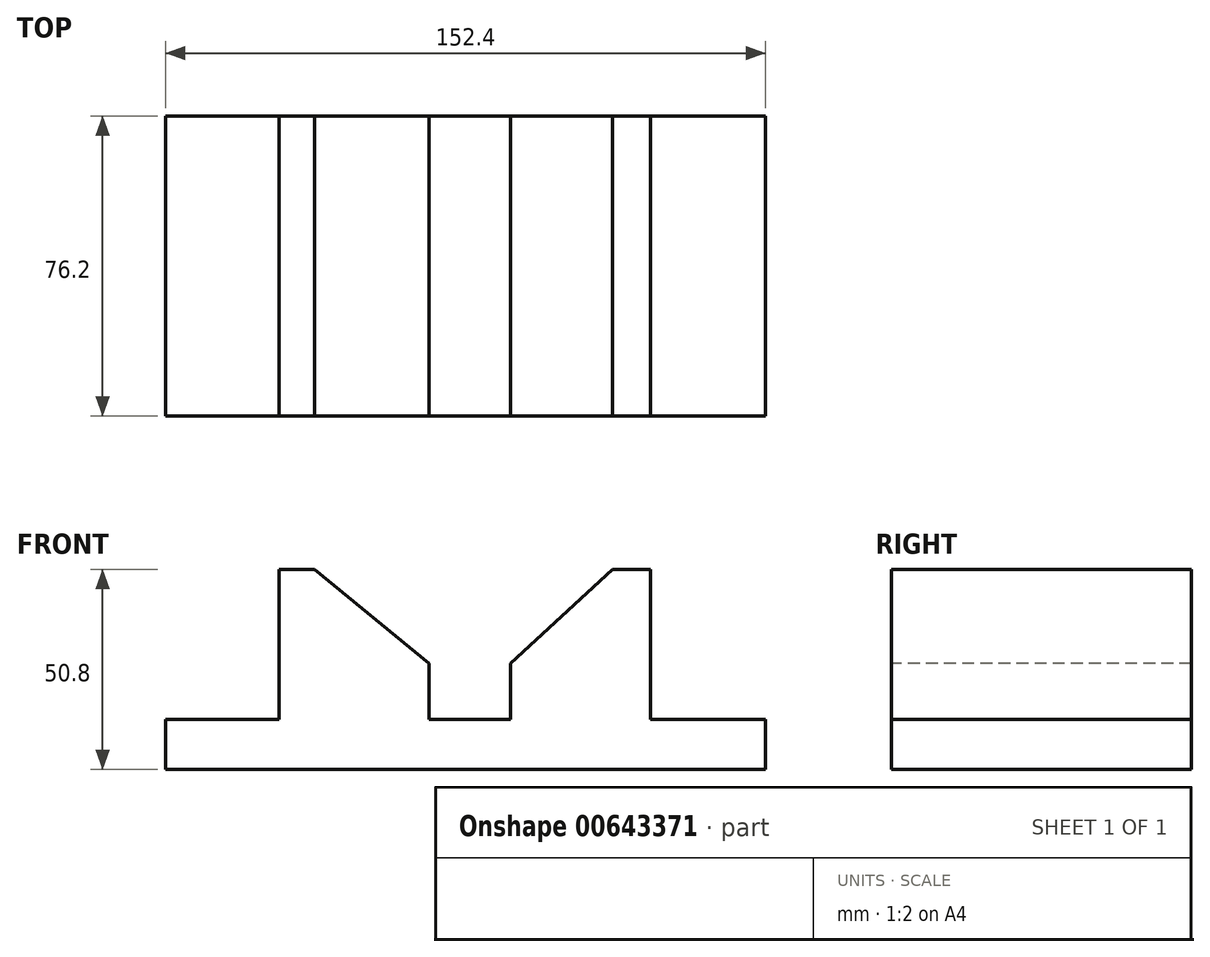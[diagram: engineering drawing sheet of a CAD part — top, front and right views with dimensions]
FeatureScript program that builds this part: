
annotation { "Feature Type Name" : "Feature", "Feature Type Description" : "" }
export const myFeature = defineFeature(function(context is Context, id is Id, definition is map)
    precondition{}
    {
        {
            var Q0;
            Q0=qCreatedBy(makeId("Top.planeOp"),FACE);
            var sketch = newSketch(context, id + "F0", { "sketchPlane" : qUnion([Q0])});
            skLineSegment(sketch, "E0.bottom", {"start": v(106.06, -5.27) * mm, "end": v(258.46, -5.27) * mm});
            skLineSegment(sketch, "E0.top", {"start": v(106.06, 70.93) * mm, "end": v(258.46, 70.93) * mm});
            skLineSegment(sketch, "E0.left", {"start": v(106.06, -5.27) * mm, "end": v(106.06, 70.93) * mm});
            skLineSegment(sketch, "E0.right", {"start": v(258.46, -5.27) * mm, "end": v(258.46, 70.93) * mm});
            skSolve(sketch);
        }
        {
            var Q0;
            Q0=makeQuery(id+"F0.imprint","IMPRINT",FACE,{"disambiguationData":[TD([[makeQuery(id+"F0.imprint","IMPRINT",EDGE,{"derivedFrom":sQuery(id+"F0.wireOp",EDGE,"E0.bottom")}),1.0]])]});
            extrude(context, id + "F1", {"entities" : qUnion([Q0]), "depth" : 12.7 * mm, "offsetDistance" : 25.4 * mm});
        }
        {
            var Q0;
            Q0=makeQuery(id+"F1.opExtrude","SWEPT_FACE",FACE,{"disambiguationData":[OSD([sQuery(id+"F0.wireOp",EDGE,"E0.bottom")])]});
            var sketch = newSketch(context, id + "F2", { "sketchPlane" : qUnion([Q0])});
            skLineSegment(sketch, "E1.bottom", {"start": v(134.92, 12.7) * mm, "end": v(173.02, 12.7) * mm});
            skLineSegment(sketch, "E1.top", {"start": v(134.92, 50.8) * mm, "end": v(173.02, 50.8) * mm});
            skLineSegment(sketch, "E1.left", {"start": v(134.92, 12.7) * mm, "end": v(134.92, 50.8) * mm});
            skLineSegment(sketch, "E1.right", {"start": v(173.02, 12.7) * mm, "end": v(173.02, 50.8) * mm});
            skSolve(sketch);
        }
        {
            var Q0;
            Q0=makeQuery(id+"F2.imprint","IMPRINT",FACE,{"disambiguationData":[TD([[makeQuery(id+"F2.imprint","IMPRINT",EDGE,{"derivedFrom":sQuery(id+"F2.wireOp",EDGE,"E1.bottom")}),1.0]])]});
            extrude(context, id + "F3", {"entities" : qUnion([Q0]), "operationType" : NewBodyOperationType.ADD, "oppositeDirection" : true, "depth" : 76.2 * mm, "offsetDistance" : 25.4 * mm});
        }
        {
            var Q0;
            Q0=makeQuery(id+"F3.boolean.opBoolean","MERGE",FACE,{"derivedFrom":[makeQuery(id+"F1.opExtrude","SWEPT_FACE",FACE,{"disambiguationData":[OSD([sQuery(id+"F0.wireOp",EDGE,"E0.bottom")])]}),makeQuery(id+"F3.opExtrude","CAP_FACE",FACE,{"disambiguationData":[OSD([sQuery(id+"F2.wireOp",EDGE,"E1.bottom"),sQuery(id+"F2.wireOp",EDGE,"E1.top"),sQuery(id+"F2.wireOp",EDGE,"E1.left"),sQuery(id+"F2.wireOp",EDGE,"E1.right")])],"isStart":true})]});
            var sketch = newSketch(context, id + "F4", { "sketchPlane" : qUnion([Q0])});
            skLineSegment(sketch, "E2.bottom", {"start": v(193.72, 12.7) * mm, "end": v(229.28, 12.7) * mm});
            skLineSegment(sketch, "E2.top", {"start": v(193.72, 50.8) * mm, "end": v(229.28, 50.8) * mm});
            skLineSegment(sketch, "E2.left", {"start": v(193.72, 12.7) * mm, "end": v(193.72, 50.8) * mm});
            skLineSegment(sketch, "E2.right", {"start": v(229.28, 12.7) * mm, "end": v(229.28, 50.8) * mm});
            skSolve(sketch);
        }
        {
            var Q0;
            Q0=makeQuery(id+"F4.imprint","IMPRINT",FACE,{"disambiguationData":[TD([[makeQuery(id+"F4.imprint","IMPRINT",EDGE,{"derivedFrom":sQuery(id+"F4.wireOp",EDGE,"E2.bottom")}),1.0]])]});
            extrude(context, id + "F5", {"entities" : qUnion([Q0]), "operationType" : NewBodyOperationType.ADD, "oppositeDirection" : true, "depth" : 76.2 * mm, "offsetDistance" : 25.4 * mm});
        }
        {
            var Q0;
            Q0=makeQuery(id+"F5.boolean.opBoolean","MERGE",FACE,{"derivedFrom":[makeQuery(id+"F3.boolean.opBoolean","MERGE",FACE,{"derivedFrom":[makeQuery(id+"F1.opExtrude","SWEPT_FACE",FACE,{"disambiguationData":[OSD([sQuery(id+"F0.wireOp",EDGE,"E0.bottom")])]}),makeQuery(id+"F3.opExtrude","CAP_FACE",FACE,{"disambiguationData":[OSD([sQuery(id+"F2.wireOp",EDGE,"E1.bottom"),sQuery(id+"F2.wireOp",EDGE,"E1.top"),sQuery(id+"F2.wireOp",EDGE,"E1.left"),sQuery(id+"F2.wireOp",EDGE,"E1.right")])],"isStart":true})]}),makeQuery(id+"F5.opExtrude","CAP_FACE",FACE,{"disambiguationData":[OSD([sQuery(id+"F4.wireOp",EDGE,"E2.bottom"),sQuery(id+"F4.wireOp",EDGE,"E2.top"),sQuery(id+"F4.wireOp",EDGE,"E2.left"),sQuery(id+"F4.wireOp",EDGE,"E2.right")])],"isStart":true})]});
            var sketch = newSketch(context, id + "F6", { "sketchPlane" : qUnion([Q0])});
            skLineSegment(sketch, "E3", {"start": v(143.86, 50.8) * mm, "end": v(173.02, 26.96) * mm});
            skLineSegment(sketch, "E4", {"start": v(173.02, 26.96) * mm, "end": v(173.02, 50.8) * mm});
            skLineSegment(sketch, "E5", {"start": v(173.02, 50.8) * mm, "end": v(143.86, 50.8) * mm});
            skSolve(sketch);
        }
        {
            var Q0;
            Q0=makeQuery(id+"F6.imprint","IMPRINT",FACE,{"disambiguationData":[TD([[makeQuery(id+"F6.imprint","IMPRINT",EDGE,{"derivedFrom":sQuery(id+"F6.wireOp",EDGE,"E3")}),1.0]])]});
            extrude(context, id + "F7", {"entities" : qUnion([Q0]), "operationType" : NewBodyOperationType.REMOVE, "oppositeDirection" : true, "depth" : 76.2 * mm, "offsetDistance" : 25.4 * mm});
        }
        {
            var Q0;
            Q0=makeQuery(id+"F5.boolean.opBoolean","MERGE",FACE,{"derivedFrom":[makeQuery(id+"F3.boolean.opBoolean","MERGE",FACE,{"derivedFrom":[makeQuery(id+"F1.opExtrude","SWEPT_FACE",FACE,{"disambiguationData":[OSD([sQuery(id+"F0.wireOp",EDGE,"E0.bottom")])]}),makeQuery(id+"F3.opExtrude","CAP_FACE",FACE,{"disambiguationData":[OSD([sQuery(id+"F2.wireOp",EDGE,"E1.bottom"),sQuery(id+"F2.wireOp",EDGE,"E1.top"),sQuery(id+"F2.wireOp",EDGE,"E1.left"),sQuery(id+"F2.wireOp",EDGE,"E1.right")])],"isStart":true})]}),makeQuery(id+"F5.opExtrude","CAP_FACE",FACE,{"disambiguationData":[OSD([sQuery(id+"F4.wireOp",EDGE,"E2.bottom"),sQuery(id+"F4.wireOp",EDGE,"E2.top"),sQuery(id+"F4.wireOp",EDGE,"E2.left"),sQuery(id+"F4.wireOp",EDGE,"E2.right")])],"isStart":true})]});
            var sketch = newSketch(context, id + "F8", { "sketchPlane" : qUnion([Q0])});
            skLineSegment(sketch, "E6", {"start": v(219.61, 50.8) * mm, "end": v(193.72, 26.96) * mm});
            skLineSegment(sketch, "E7", {"start": v(193.72, 26.96) * mm, "end": v(193.72, 50.8) * mm});
            skLineSegment(sketch, "E8", {"start": v(193.72, 50.8) * mm, "end": v(219.61, 50.8) * mm});
            skSolve(sketch);
        }
        {
            var Q0;
            Q0=makeQuery(id+"F8.imprint","IMPRINT",FACE,{"disambiguationData":[TD([[makeQuery(id+"F8.imprint","IMPRINT",EDGE,{"derivedFrom":sQuery(id+"F8.wireOp",EDGE,"E6")}),-1.0]])]});
            extrude(context, id + "F9", {"entities" : qUnion([Q0]), "operationType" : NewBodyOperationType.REMOVE, "oppositeDirection" : true, "depth" : 76.2 * mm, "offsetDistance" : 25.4 * mm});
        }
    });
